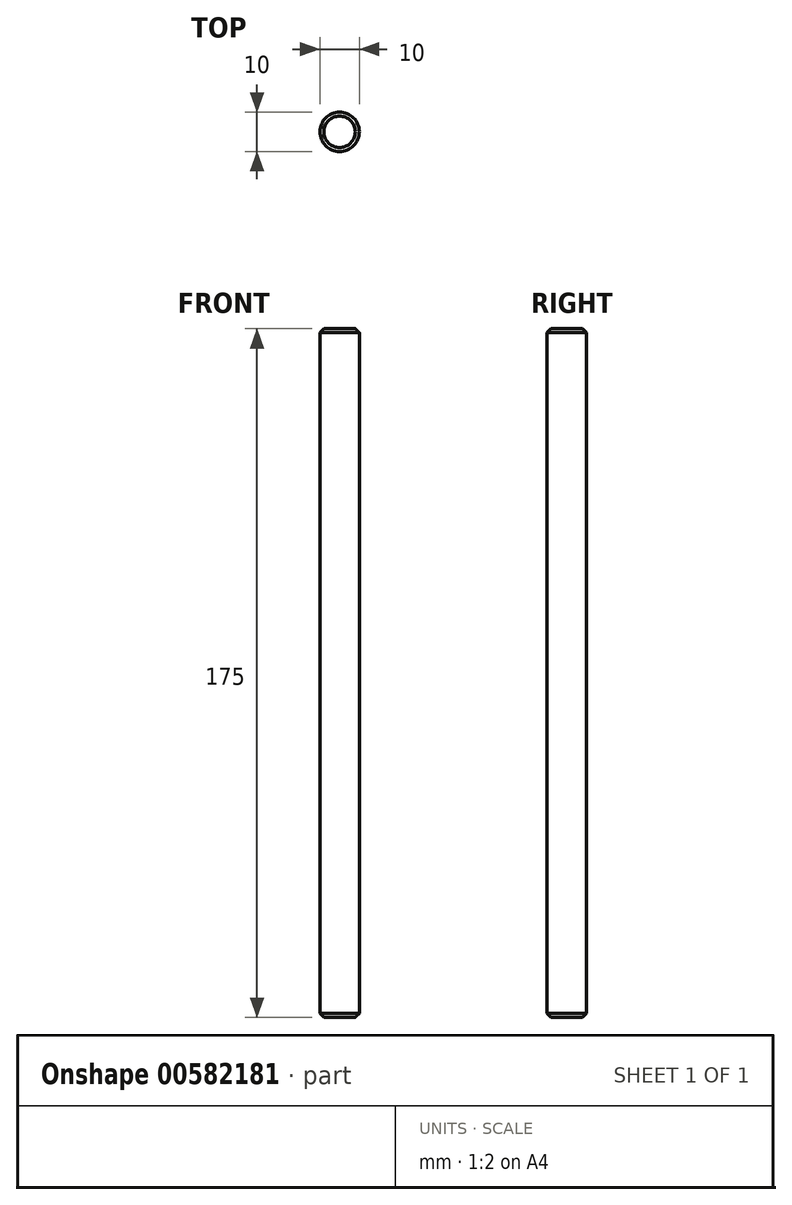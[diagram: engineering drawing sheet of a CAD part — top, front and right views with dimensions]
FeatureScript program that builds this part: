
annotation { "Feature Type Name" : "Feature", "Feature Type Description" : "" }
export const myFeature = defineFeature(function(context is Context, id is Id, definition is map)
    precondition{}
    {
        {
            var Q0;
            Q0=qCreatedBy(makeId("Top.planeOp"),FACE);
            var sketch = newSketch(context, id + "F0", { "sketchPlane" : qUnion([Q0])});
            skCircle(sketch, "E0", {"center": v(0, 0) * mm, "radius": 5 * mm});
            skSolve(sketch);
        }
        {
            var Q0;
            Q0=qSketchRegion(id+"F0",true);
            extrude(context, id + "F1", {"entities" : qUnion([Q0]), "depth" : 175 * mm, "offsetDistance" : 25 * mm});
        }
        {
            var Q0;
            Q0=makeQuery(id+"F1.opExtrude","CAP_EDGE",EDGE,{"disambiguationData":[OSD([sQuery(id+"F0.wireOp",EDGE,"E0")])],"isStart":false});
            var Q1;
            Q1=makeQuery(id+"F1.opExtrude","CAP_EDGE",EDGE,{"disambiguationData":[OSD([sQuery(id+"F0.wireOp",EDGE,"E0")])],"isStart":true});
            chamfer(context, id + "F2", {"entities" : qUnion([Q0, Q1]), "width" : 1 * mm, "tangentPropagation" : true});
        }
    });
